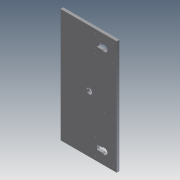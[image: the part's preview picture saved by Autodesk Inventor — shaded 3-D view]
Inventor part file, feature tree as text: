
AUTODESK INVENTOR PART (.ipt)
format: ipt  version: 2011 (Build 150239000, 239)  size: 531,456 bytes
history: native  units: in
note: dims shown in document units (in); Inventor stores cm internally (conversion verified against a paired STEP export)
features: extrude x48, sketch x48, fillet x1
ambient origin geometry x8: Origin, YZ Plane, XZ Plane, XY Plane, X Axis, Y Axis, Z Axis, Center Point
bodies: Solid1 (feature_tree)
feature tree (97):
  extrude  "Extrusion1"  Depth=4.0in
  extrude  "Extrusion2"  Depth=2.16in
  extrude  "Extrusion3"  Depth=1.7655in
  extrude  "Extrusion4"  Depth=0.029in TaperAngle=0.0deg
  extrude  "Extrusion5"  Depth=2.36in
  fillet  "Fillet1"  Radius=2.56in
  extrude  "Extrusion6"  Depth=0.125in
  extrude  "Extrusion7"  Depth=0.262in TaperAngle=0.0deg
  extrude  "Extrusion8"  Depth=0.029in TaperAngle=0.0deg
  extrude  "Extrusion9"  Depth=0.156in
  extrude  "Extrusion10"  Depth=0.5in TaperAngle=0.0deg
  extrude  "Extrusion11"  Depth=0.5in TaperAngle=0.0deg
  extrude  "Extrusion12"  Depth=1.875in TaperAngle=0.0deg
  extrude  "Extrusion13"  Depth=2.125in TaperAngle=0.0deg
  sketch  "Sketch14"  dims[d44=2.125in d45=0.0in d46=2.125in d47=0.0in]
  sketch  "Sketch15"  dims[d48=2.125in d49=0.0in d50=1.875in d51=0.0in]
  sketch  "Sketch16"  dims[d52=2.125in d53=0.0in d54=2.125in d55=0.0in]
  sketch  "Sketch17"  dims[d56=1.875in d57=0.0in d58=1.875in d59=0.0in]
  extrude  "Extrusion14"  Depth=2.125in TaperAngle=0.0deg
  extrude  "Extrusion15"  Depth=1.875in TaperAngle=0.0deg
  extrude  "Extrusion16"  Depth=2.125in TaperAngle=0.0deg
  extrude  "Extrusion17"  Depth=1.875in TaperAngle=0.0deg
  extrude  "Extrusion18"  Depth=2.125in TaperAngle=0.0deg
  extrude  "Extrusion19"  Depth=6.248in TaperAngle=0.0deg
  extrude  "Extrusion20"  Depth=1.281in
  extrude  "Extrusion21"  Depth=7.0in TaperAngle=0.0deg
  extrude  "Extrusion22"  Depth=0.25in TaperAngle=0.0deg
  extrude  "Extrusion23"  Depth=0.25in TaperAngle=0.0deg
  extrude  "Extrusion24"  Depth=0.25in TaperAngle=0.0deg
  extrude  "Extrusion25"  Depth=0.25in TaperAngle=0.0deg
  extrude  "Extrusion26"  Depth=0.875in
  extrude  "Extrusion27"  Depth=0.875in
  extrude  "Extrusion28"  Depth=1.0in TaperAngle=0.0deg
  extrude  "Extrusion29"  Depth=0.5in TaperAngle=0.0deg
  extrude  "Extrusion30"  Depth=0.4134in
  extrude  "Extrusion31"  Depth=0.8268in
  extrude  "Extrusion32"  Depth=0.8268in
  extrude  "Extrusion33"  Depth=0.9055in
  extrude  "Extrusion34"  Depth=1.1024in
  extrude  "Extrusion35"  Depth=1.0in TaperAngle=0.0deg
  extrude  "Extrusion36"  Depth=3.0in
  extrude  "Extrusion37"  Depth=0.5in
  extrude  "Extrusion38"  Depth=0.5in
  extrude  "Extrusion39"  Depth=0.75in
  extrude  "Extrusion40"  Depth=0.75in
  extrude  "Extrusion41"  Depth=0.156in
  extrude  "Extrusion42"  Depth=1.0in TaperAngle=0.0deg
  extrude  "Extrusion43"  Depth=1.0in
  extrude  "Extrusion44"  Depth=0.5315in
  extrude  "Extrusion45"  Depth=0.315in
  extrude  "Extrusion46"  Depth=0.315in
  extrude  "Extrusion47"  Depth=0.0787in
  extrude  "Extrusion48"  Depth=0.5315in
  sketch  "Sketch1"  dims[d0=4.0in d1=4.0in]
  sketch  "Sketch2"  dims[d2=0.029in d3=0.0in d4=2.16in]
  sketch  "Sketch3"  dims[d5=0.029in d6=0.0in d7=1.7655in]
  sketch  "Sketch4"  dims[d8=0.156in d9=0.029in d10=0.0in]
  sketch  "Sketch5"  dims[d11=0.029in d12=0.0in d13=2.36in d14=2.56in]
  sketch  "Sketch6"  dims[d15=0.262in d16=0.0in d17=0.125in]
  sketch  "Sketch7"  dims[d18=0.362in d19=0.0in d20=0.262in d21=0.0in]
  sketch  "Sketch8"  dims[d22=0.1in d23=0.0in d24=0.029in d25=0.0in]
  sketch  "Sketch9"  dims[d26=1.594in d27=0.156in]
  sketch  "Sketch10"  dims[d28=0.029in d29=0.0in d30=0.5in d31=0.0in]
  sketch  "Sketch11"  dims[d32=0.75in d33=0.0in d34=0.5in d35=0.0in]
  sketch  "Sketch12"  dims[d36=2.125in d37=0.0in d38=1.875in d39=0.0in]
  sketch  "Sketch13"  dims[d40=1.875in d41=0.0in d42=2.125in d43=0.0in]
  sketch  "Sketch18"  dims[d60=2.125in d61=0.0in d62=2.125in d63=0.0in]
  sketch  "Sketch19"  dims[d64=0.875in d65=0.0in d66=6.248in d67=0.0in]
  sketch  "Sketch20"  dims[d68=7.0in d69=0.0in d70=1.281in]
  sketch  "Sketch21"  dims[d71=3.188in d72=7.0in d73=0.0in]
  sketch  "Sketch22"  dims[d74=0.25in d75=0.0in d76=0.25in d77=0.0in]
  sketch  "Sketch23"  dims[d78=0.25in d79=0.0in d80=0.25in d81=0.0in]
  sketch  "Sketch24"  dims[d82=0.25in d83=0.0in d84=0.25in d85=0.0in]
  sketch  "Sketch25"  dims[d86=3.875in d87=0.0in d88=0.25in d89=0.0in]
  sketch  "Sketch26"  dims[d90=0.25in d91=0.0in d92=0.875in]
  sketch  "Sketch27"  dims[d93=0.875in d94=0.875in]
  sketch  "Sketch28"  dims[d95=0.875in d96=1.0in d97=0.0in]
  sketch  "Sketch29"  dims[d98=0.25in d99=0.0in d100=0.5in d101=0.0in]
  sketch  "Sketch30"  dims[d102=0.8858in d103=0.4134in]
  sketch  "Sketch31"  dims[d104=1.378in d105=0.8268in]
  sketch  "Sketch32"  dims[d106=0.4134in d107=0.8268in]
  sketch  "Sketch33"  dims[d108=0.9055in d109=0.9055in]
  sketch  "Sketch34"  dims[d110=0.5in d111=0.0in d112=1.1024in]
  sketch  "Sketch35"  dims[d113=1.1024in d114=1.0in d115=0.0in]
  sketch  "Sketch36"  dims[d116=2.75in d117=3.0in]
  sketch  "Sketch37"  dims[d118=5.5in d119=0.5in]
  sketch  "Sketch38"  dims[d120=0.5in d121=0.5in]
  sketch  "Sketch39"  dims[d122=0.5in d123=0.75in]
  sketch  "Sketch40"  dims[d124=0.75in d125=0.75in]
  sketch  "Sketch41"  dims[d126=0.75in d127=0.156in]
  sketch  "Sketch42"  dims[d128=0.156in d129=1.0in d130=0.0in]
  sketch  "Sketch43"  dims[d131=5.0in d132=1.0in]
  sketch  "Sketch44"  dims[d133=1.0in d134=0.0in d135=0.5315in]
  sketch  "Sketch45"  dims[d136=0.2559in d137=0.315in]
  sketch  "Sketch46"  dims[d138=0.315in d139=0.315in]
  sketch  "Sketch47"  dims[d140=0.0787in d141=0.0787in]
  sketch  "Sketch48"  dims[d142=1.063in d143=0.5315in d144=0.5709in d145=0.6299in d146=1.063in d147=1.0in d148=0.0in]
